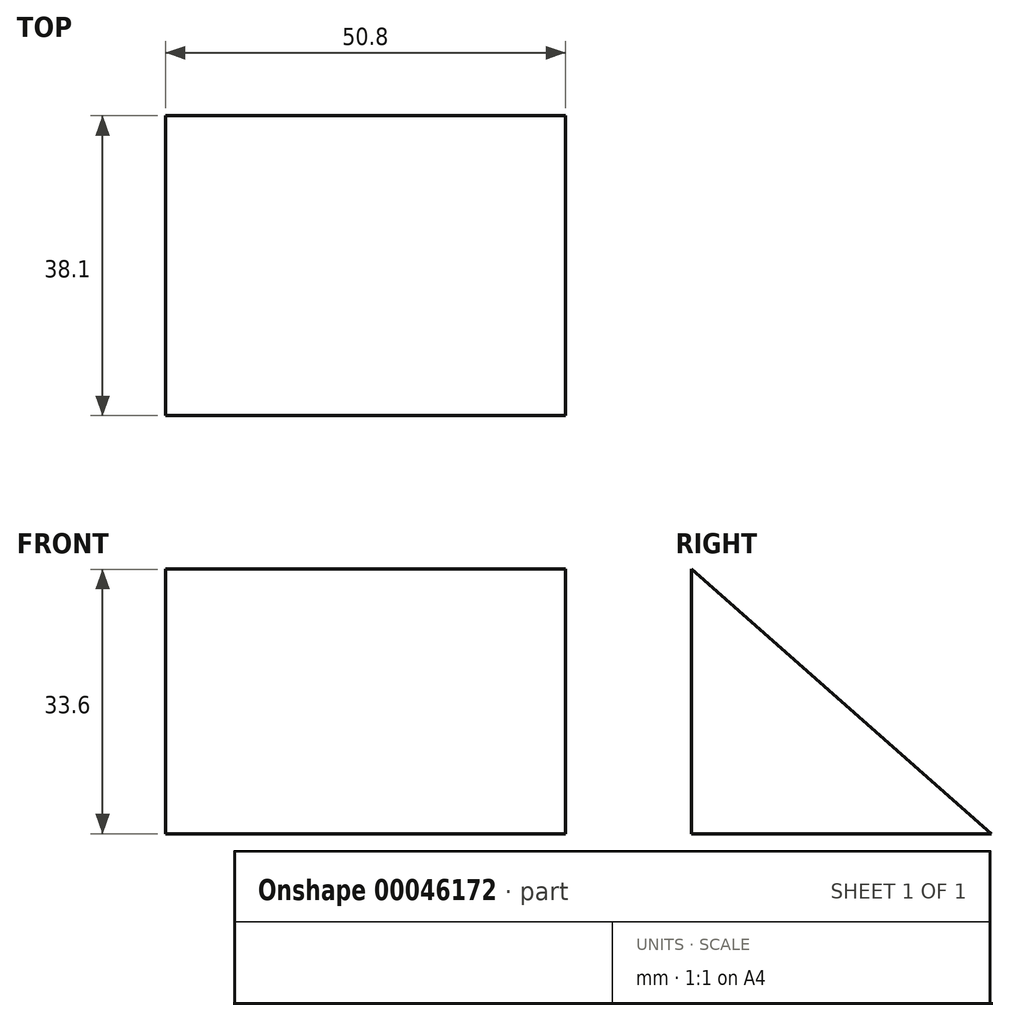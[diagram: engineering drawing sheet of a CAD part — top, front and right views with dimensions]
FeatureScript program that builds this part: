
annotation { "Feature Type Name" : "Feature", "Feature Type Description" : "" }
export const myFeature = defineFeature(function(context is Context, id is Id, definition is map)
    precondition{}
    {
        {
            var Q0;
            Q0=qCreatedBy(makeId("Right.planeOp"),FACE);
            var sketch = newSketch(context, id + "F0", { "sketchPlane" : qUnion([Q0])});
            skLineSegment(sketch, "E0", {"start": v(0, 0) * mm, "end": v(0, 33.6) * mm});
            skLineSegment(sketch, "E1", {"start": v(0, 33.6) * mm, "end": v(38.1, 0) * mm});
            skLineSegment(sketch, "E2", {"start": v(38.1, 0) * mm, "end": v(0, 0) * mm});
            skSolve(sketch);
        }
        {
            var Q0;
            Q0=makeQuery(id+"F0.imprint","IMPRINT",FACE,{"disambiguationData":[TD([[makeQuery(id+"F0.imprint","IMPRINT",EDGE,{"derivedFrom":sQuery(id+"F0.wireOp",EDGE,"E0")}),-1.0]])]});
            extrude(context, id + "F1", {"entities" : qUnion([Q0]), "depth" : 50.8 * mm});
        }
    });
